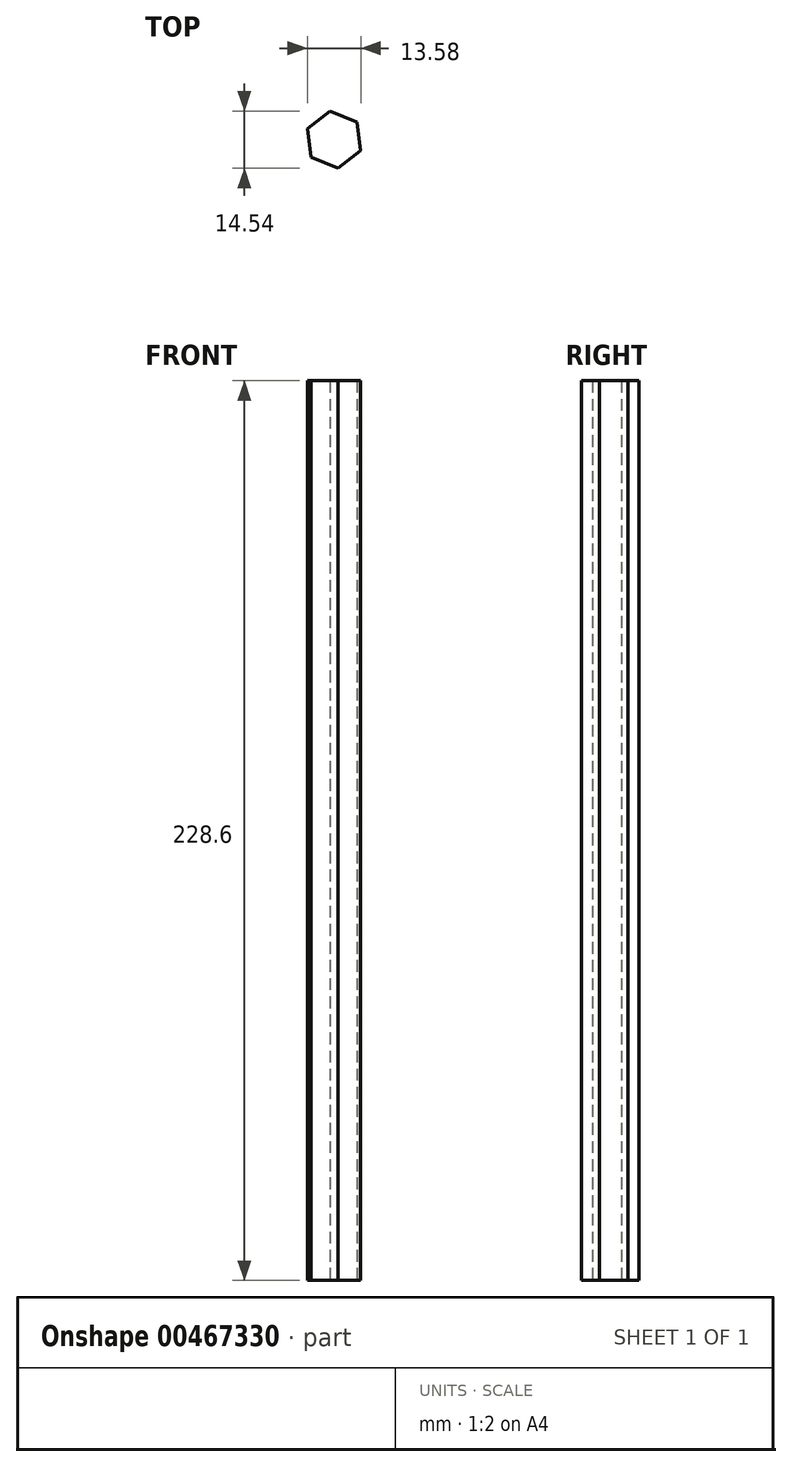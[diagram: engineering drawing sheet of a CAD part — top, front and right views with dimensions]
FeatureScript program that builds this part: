
annotation { "Feature Type Name" : "Feature", "Feature Type Description" : "" }
export const myFeature = defineFeature(function(context is Context, id is Id, definition is map)
    precondition{}
    {
        {
            var Q0;
            Q0=qCreatedBy(makeId("Top.planeOp"),FACE);
            var sketch = newSketch(context, id + "F0", { "sketchPlane" : qUnion([Q0])});
            skCircle(sketch, "E0.cCircle", {"center": v(0, 0) * mm, "radius": 6.35 * mm, "construction": true});
            skLineSegment(sketch, "E0.0", {"start": v(-0.99, 7.27) * mm, "end": v(5.8, 4.49) * mm});
            skLineSegment(sketch, "E0.1", {"start": v(5.8, 4.49) * mm, "end": v(6.79, -2.78) * mm});
            skLineSegment(sketch, "E0.2", {"start": v(6.79, -2.78) * mm, "end": v(0.99, -7.27) * mm});
            skLineSegment(sketch, "E0.3", {"start": v(0.99, -7.27) * mm, "end": v(-5.8, -4.49) * mm});
            skLineSegment(sketch, "E0.4", {"start": v(-5.8, -4.49) * mm, "end": v(-6.79, 2.78) * mm});
            skLineSegment(sketch, "E0.5", {"start": v(-6.79, 2.78) * mm, "end": v(-0.99, 7.27) * mm});
            skPoint(sketch, "E0.0.midPoint", {"position": v(2.4, 5.88) * mm});
            skSolve(sketch);
        }
        {
            var Q0;
            Q0=makeQuery(id+"F0.imprint","IMPRINT",FACE,{"disambiguationData":[TD([[makeQuery(id+"F0.imprint","IMPRINT",EDGE,{"derivedFrom":sQuery(id+"F0.wireOp",EDGE,"E0.0")}),-1.0]])]});
            extrude(context, id + "F1", {"entities" : qUnion([Q0]), "depth" : 228.6 * mm});
        }
    });
